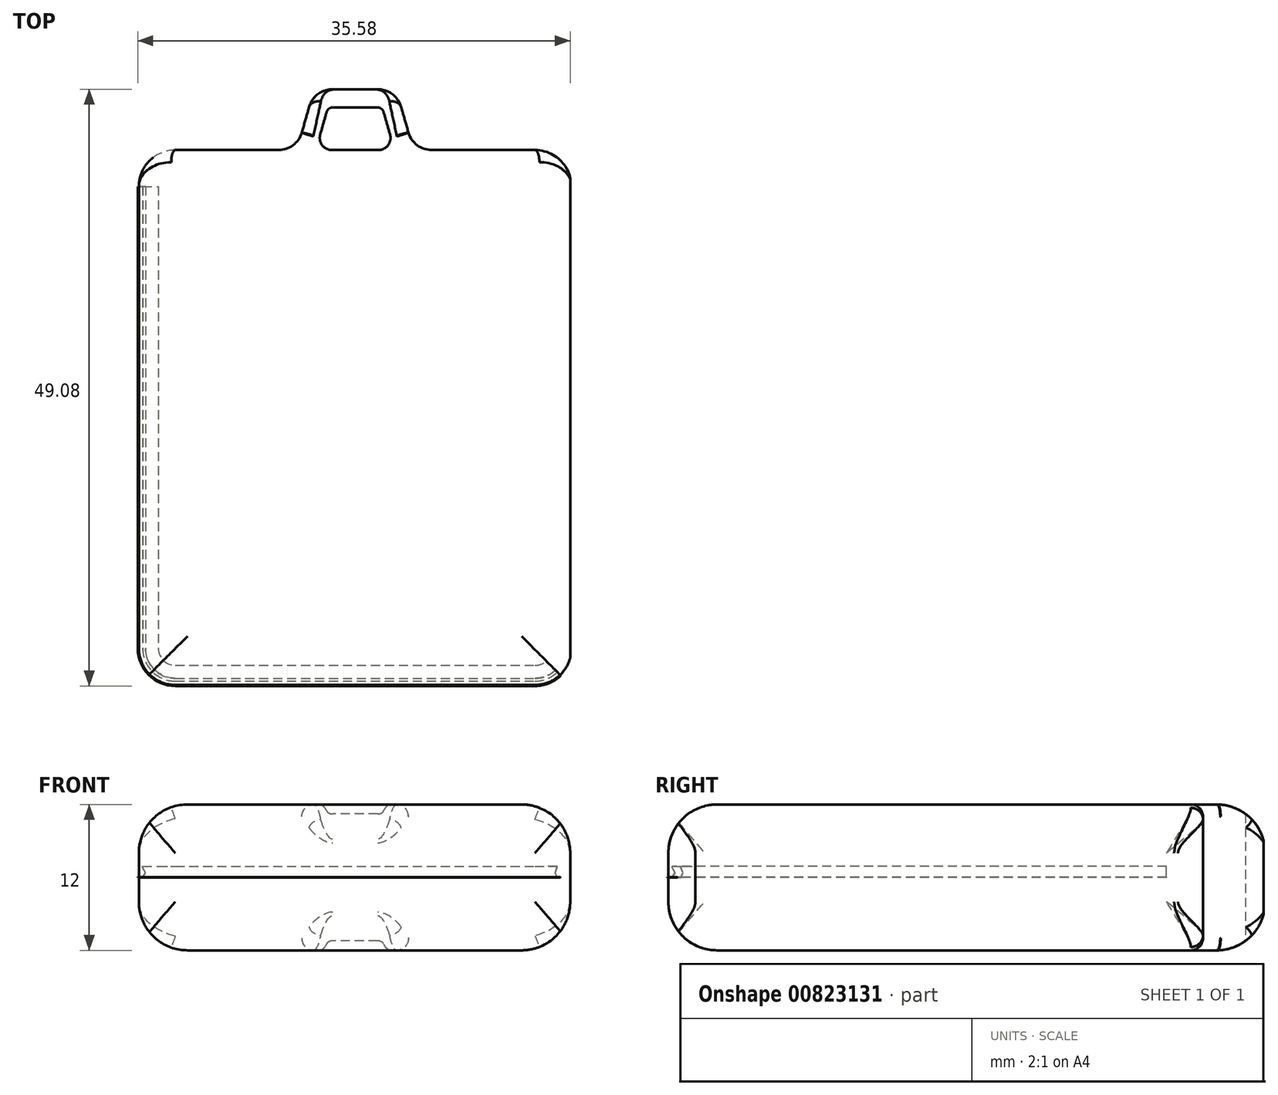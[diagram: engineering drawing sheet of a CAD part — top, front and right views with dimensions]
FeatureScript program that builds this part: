
annotation { "Feature Type Name" : "Feature", "Feature Type Description" : "" }
export const myFeature = defineFeature(function(context is Context, id is Id, definition is map)
    precondition{}
    {
        {
            var Q0;
            Q0=qCreatedBy(makeId("Top.planeOp"),FACE);
            var sketch = newSketch(context, id + "F0", { "sketchPlane" : qUnion([Q0])});
            skLineSegment(sketch, "E0.bottom", {"start": v(3, 0) * mm, "end": v(32.6, 0) * mm});
            skLineSegment(sketch, "E0.top", {"start": v(3, 44) * mm, "end": v(11.5, 44) * mm});
            skLineSegment(sketch, "E0.left", {"start": v(0, 3) * mm, "end": v(0, 41) * mm});
            skLineSegment(sketch, "E0.right", {"start": v(35.6, 3) * mm, "end": v(35.6, 41) * mm});
            skLineSegment(sketch, "E1", {"start": v(17.8, 62.18) * mm, "end": v(17.8, 0) * mm, "construction": true});
            skLineSegment(sketch, "E2", {"start": v(13.42, 45.45) * mm, "end": v(14.02, 47.55) * mm});
            skLineSegment(sketch, "E3", {"start": v(15.94, 49) * mm, "end": v(19.66, 49) * mm});
            skLineSegment(sketch, "E4", {"start": v(21.58, 47.55) * mm, "end": v(22.18, 45.45) * mm});
            skLineSegment(sketch, "E5.trimOffspring", {"start": v(24.1, 44) * mm, "end": v(32.6, 44) * mm});
            skPoint(sketch, "E6.visualSharp", {"position": v(13, 44) * mm});
            skArc(sketch, "E6.filletArc", {"start": v(11.5, 44) * mm, "mid": v(12.7, 44.4) * mm, "end": v(13.42, 45.45) * mm});
            skPoint(sketch, "E7.visualSharp", {"position": v(14.43, 49) * mm});
            skArc(sketch, "E7.filletArc", {"start": v(15.94, 49) * mm, "mid": v(14.74, 48.6) * mm, "end": v(14.02, 47.55) * mm});
            skPoint(sketch, "E8.visualSharp", {"position": v(21.17, 49) * mm});
            skArc(sketch, "E8.filletArc", {"start": v(21.58, 47.55) * mm, "mid": v(20.86, 48.6) * mm, "end": v(19.66, 49) * mm});
            skPoint(sketch, "E9.visualSharp", {"position": v(22.6, 44) * mm});
            skArc(sketch, "E9.filletArc", {"start": v(22.18, 45.45) * mm, "mid": v(22.9, 44.4) * mm, "end": v(24.1, 44) * mm});
            skLineSegment(sketch, "E10.0", {"start": v(15.94, 47.5) * mm, "end": v(19.66, 47.5) * mm});
            skLineSegment(sketch, "E11.0", {"start": v(14.93, 45.28) * mm, "end": v(15.46, 47.14) * mm});
            skLineSegment(sketch, "E12.0", {"start": v(20.14, 47.14) * mm, "end": v(20.67, 45.28) * mm});
            skLineSegment(sketch, "E13", {"start": v(15.89, 44) * mm, "end": v(19.71, 44) * mm});
            skPoint(sketch, "E14.visualSharp", {"position": v(15.56, 47.5) * mm});
            skArc(sketch, "E14.filletArc", {"start": v(15.94, 47.5) * mm, "mid": v(15.64, 47.4) * mm, "end": v(15.46, 47.14) * mm});
            skArc(sketch, "E15.filletArc", {"start": v(20.14, 47.14) * mm, "mid": v(19.96, 47.4) * mm, "end": v(19.66, 47.5) * mm});
            skPoint(sketch, "E16.visualSharp", {"position": v(21.04, 44) * mm});
            skArc(sketch, "E16.filletArc", {"start": v(19.71, 44) * mm, "mid": v(20.51, 44.4) * mm, "end": v(20.67, 45.28) * mm});
            skPoint(sketch, "E17.visualSharp", {"position": v(14.56, 44) * mm});
            skArc(sketch, "E17.filletArc", {"start": v(14.93, 45.28) * mm, "mid": v(15.09, 44.4) * mm, "end": v(15.89, 44) * mm});
            skPoint(sketch, "E18.visualSharp", {"position": v(0, 44) * mm});
            skArc(sketch, "E18.filletArc", {"start": v(3, 44) * mm, "mid": v(0.88, 43.12) * mm, "end": v(0, 41) * mm});
            skPoint(sketch, "E19.visualSharp", {"position": v(35.6, 44) * mm});
            skArc(sketch, "E19.filletArc", {"start": v(35.6, 41) * mm, "mid": v(34.72, 43.12) * mm, "end": v(32.6, 44) * mm});
            skPoint(sketch, "E20.visualSharp", {"position": v(35.6, 0) * mm});
            skArc(sketch, "E20.filletArc", {"start": v(32.6, 0) * mm, "mid": v(34.72, 0.88) * mm, "end": v(35.6, 3) * mm});
            skPoint(sketch, "E21.visualSharp", {"position": v(0, 0) * mm});
            skArc(sketch, "E21.filletArc", {"start": v(0, 3) * mm, "mid": v(0.88, 0.88) * mm, "end": v(3, 0) * mm});
            skSolve(sketch);
        }
        {
            var Q0;
            Q0 = qSketchRegion(id + "F0", true);
            extrude(context, id + "F1", {"entities" : qUnion([Q0]), "depth" : 12 * mm, "offsetDistance" : 25 * mm});
        }
        {
            var Q0;
            Q0=qCreatedBy(makeId("Front.planeOp"),FACE);
            var sketch = newSketch(context, id + "F2", { "sketchPlane" : qUnion([Q0])});
            skLineSegment(sketch, "E22.bottom", {"start": v(4, 0) * mm, "end": v(31.5, 0) * mm});
            skLineSegment(sketch, "E22.top", {"start": v(4, 12) * mm, "end": v(31.5, 12) * mm});
            skLineSegment(sketch, "E22.left", {"start": v(0, 4) * mm, "end": v(0, 8) * mm});
            skLineSegment(sketch, "E22.right", {"start": v(35.5, 4) * mm, "end": v(35.5, 8) * mm});
            skPoint(sketch, "E23.visualSharp", {"position": v(0, 12) * mm});
            skArc(sketch, "E23.filletArc", {"start": v(4, 12) * mm, "mid": v(1.17, 10.83) * mm, "end": v(0, 8) * mm});
            skPoint(sketch, "E24.visualSharp", {"position": v(0, 0) * mm});
            skArc(sketch, "E24.filletArc", {"start": v(0, 4) * mm, "mid": v(1.17, 1.17) * mm, "end": v(4, 0) * mm});
            skPoint(sketch, "E25.visualSharp", {"position": v(35.5, 0) * mm});
            skArc(sketch, "E25.filletArc", {"start": v(31.5, 0) * mm, "mid": v(34.33, 1.17) * mm, "end": v(35.5, 4) * mm});
            skPoint(sketch, "E26.visualSharp", {"position": v(35.5, 12) * mm});
            skArc(sketch, "E26.filletArc", {"start": v(35.5, 8) * mm, "mid": v(34.33, 10.83) * mm, "end": v(31.5, 12) * mm});
            skLineSegment(sketch, "E27.bottom", {"start": v(-3.14, 13.75) * mm, "end": v(38.49, 13.75) * mm});
            skLineSegment(sketch, "E27.top", {"start": v(-3.14, -2.53) * mm, "end": v(38.49, -2.53) * mm});
            skLineSegment(sketch, "E27.left", {"start": v(-3.14, 13.75) * mm, "end": v(-3.14, -2.53) * mm});
            skLineSegment(sketch, "E27.right", {"start": v(38.49, 13.75) * mm, "end": v(38.49, -2.53) * mm});
            skSolve(sketch);
        }
        {
            var Q0;
            Q0 = qSketchRegion(id + "F2", true);
            extrude(context, id + "F3", {"entities" : qUnion([Q0]), "operationType" : NewBodyOperationType.REMOVE, "endBound" : BoundingType.THROUGH_ALL, "oppositeDirection" : true, "depth" : 25 * mm, "offsetDistance" : 25 * mm});
        }
        {
            var Q0;
            Q0=qCreatedBy(makeId("Right.planeOp"),FACE);
            var sketch = newSketch(context, id + "F4", { "sketchPlane" : qUnion([Q0])});
            skLineSegment(sketch, "E28.bottom", {"start": v(4, 0) * mm, "end": v(45.12, 0) * mm});
            skLineSegment(sketch, "E28.top", {"start": v(4, 12) * mm, "end": v(45.12, 12) * mm});
            skLineSegment(sketch, "E28.left", {"start": v(0, 4) * mm, "end": v(0, 8) * mm});
            skLineSegment(sketch, "E28.right", {"start": v(49.12, 4) * mm, "end": v(49.12, 8) * mm});
            skPoint(sketch, "E29.visualSharp", {"position": v(49.12, 0) * mm});
            skArc(sketch, "E29.filletArc", {"start": v(45.12, 0) * mm, "mid": v(47.95, 1.17) * mm, "end": v(49.12, 4) * mm});
            skPoint(sketch, "E30.visualSharp", {"position": v(0, 0) * mm});
            skArc(sketch, "E30.filletArc", {"start": v(0, 4) * mm, "mid": v(1.17, 1.17) * mm, "end": v(4, 0) * mm});
            skPoint(sketch, "E31.visualSharp", {"position": v(0, 12) * mm});
            skArc(sketch, "E31.filletArc", {"start": v(4, 12) * mm, "mid": v(1.17, 10.83) * mm, "end": v(0, 8) * mm});
            skPoint(sketch, "E32.visualSharp", {"position": v(49.12, 12) * mm});
            skArc(sketch, "E32.filletArc", {"start": v(49.12, 8) * mm, "mid": v(47.95, 10.83) * mm, "end": v(45.12, 12) * mm});
            skLineSegment(sketch, "E33.bottom", {"start": v(51.83, -3.61) * mm, "end": v(-3.85, -3.61) * mm});
            skLineSegment(sketch, "E33.top", {"start": v(51.83, 17.86) * mm, "end": v(-3.85, 17.86) * mm});
            skLineSegment(sketch, "E33.left", {"start": v(51.83, -3.61) * mm, "end": v(51.83, 17.86) * mm});
            skLineSegment(sketch, "E33.right", {"start": v(-3.85, -3.61) * mm, "end": v(-3.85, 17.86) * mm});
            skSolve(sketch);
        }
        {
            var Q0;
            Q0 = qSketchRegion(id + "F4", true);
            extrude(context, id + "F5", {"entities" : qUnion([Q0]), "operationType" : NewBodyOperationType.REMOVE, "endBound" : BoundingType.THROUGH_ALL, "depth" : 25 * mm, "offsetDistance" : 25 * mm});
        }
        {
            var Q0;
            Q0=makeQuery(id+"F1.opExtrude","CAP_EDGE",EDGE,{"disambiguationData":[OSD([sQuery(id+"F0.wireOp",EDGE,"E0.top")])],"isStart":true});
            var Q1;
            Q1=makeQuery(id+"F1.opExtrude","CAP_EDGE",EDGE,{"disambiguationData":[OSD([sQuery(id+"F0.wireOp",EDGE,"E5.trimOffspring")])],"isStart":true});
            var Q2;
            Q2=makeQuery(id+"F1.opExtrude","CAP_EDGE",EDGE,{"disambiguationData":[OSD([sQuery(id+"F0.wireOp",EDGE,"E5.trimOffspring")])],"isStart":false});
            var Q3;
            Q3=makeQuery(id+"F1.opExtrude","CAP_EDGE",EDGE,{"disambiguationData":[OSD([sQuery(id+"F0.wireOp",EDGE,"E0.top")])],"isStart":false});
            fillet(context, id + "F6", {"entities" : qUnion([Q0, Q1, Q2, Q3]), "radius" : 1 * mm, "tangentPropagation" : true, "allowEdgeOverflow" : false});
        }
        {
            var Q0;
            Q0=qCreatedBy(makeId("Top.planeOp"),FACE);
            cPlane(context, id + "F7", {"entities" : qUnion([Q0]), "cplaneType" : CPlaneType.OFFSET, "offset" : 6 * mm, "width" : 150 * mm, "height" : 150 * mm});
        }
        {
            var Q0;
            Q0=qCreatedBy(makeId("Front.planeOp"),FACE);
            cPlane(context, id + "F8", {"entities" : qUnion([Q0]), "cplaneType" : CPlaneType.OFFSET, "offset" : 20 * mm, "oppositeDirection" : true, "width" : 150 * mm, "height" : 150 * mm});
        }
        {
            var Q0;
            Q0=qCreatedBy(id+"F8.planeOp",FACE);
            var sketch = newSketch(context, id + "F9", { "sketchPlane" : qUnion([Q0])});
            skLineSegment(sketch, "E34", {"start": v(0.31, 6) * mm, "end": v(0.54, 6.36) * mm});
            skLineSegment(sketch, "E35", {"start": v(0.54, 6.36) * mm, "end": v(0.31, 6.82) * mm});
            skLineSegment(sketch, "E36.0", {"start": v(0.32, 6) * mm, "end": v(0.55, 6.36) * mm});
            skLineSegment(sketch, "E37.0", {"start": v(0.55, 6.36) * mm, "end": v(0.32, 6.82) * mm});
            skLineSegment(sketch, "E38", {"start": v(0.32, 6.92) * mm, "end": v(1.6, 6.92) * mm});
            skLineSegment(sketch, "E39.0", {"start": v(0.32, 6.82) * mm, "end": v(0.32, 6.9) * mm});
            skLineSegment(sketch, "E40.0", {"start": v(0.32, 6.9) * mm, "end": v(1.6, 6.9) * mm});
            skLineSegment(sketch, "E41", {"start": v(0.31, 6.82) * mm, "end": v(0.31, 6.91) * mm});
            skLineSegment(sketch, "E42", {"start": v(0.31, 6) * mm, "end": v(-0.08, 6) * mm});
            skLineSegment(sketch, "E43", {"start": v(-0.08, 6) * mm, "end": v(-0.08, 6) * mm});
            skLineSegment(sketch, "E44", {"start": v(-0.08, 6) * mm, "end": v(0.32, 6) * mm});
            skPoint(sketch, "E45.visualSharp", {"position": v(0.32, 6.9) * mm});
            skArc(sketch, "E45.filletArc", {"start": v(0.32, 6.9) * mm, "mid": v(0.32, 6.9) * mm, "end": v(0.32, 6.9) * mm});
            skPoint(sketch, "E46.visualSharp", {"position": v(0.31, 6.92) * mm});
            skPoint(sketch, "E47.visualSharp", {"position": v(0.31, 6.82) * mm});
            skArc(sketch, "E47.filletArc", {"start": v(0.31, 6.82) * mm, "mid": v(0.31, 6.82) * mm, "end": v(0.31, 6.82) * mm});
            skPoint(sketch, "E48.visualSharp", {"position": v(0.32, 6.82) * mm});
            skArc(sketch, "E48.filletArc", {"start": v(0.32, 6.82) * mm, "mid": v(0.32, 6.82) * mm, "end": v(0.32, 6.82) * mm});
            skPoint(sketch, "E49.visualSharp", {"position": v(0.54, 6.36) * mm});
            skArc(sketch, "E49.filletArc", {"start": v(0.54, 6.36) * mm, "mid": v(0.54, 6.36) * mm, "end": v(0.54, 6.36) * mm});
            skPoint(sketch, "E50.visualSharp", {"position": v(0.55, 6.36) * mm});
            skArc(sketch, "E50.filletArc", {"start": v(0.55, 6.36) * mm, "mid": v(0.55, 6.36) * mm, "end": v(0.55, 6.36) * mm});
            skPoint(sketch, "E51.visualSharp", {"position": v(0.31, 6) * mm});
            skArc(sketch, "E51.filletArc", {"start": v(0.31, 6) * mm, "mid": v(0.31, 6) * mm, "end": v(0.31, 6) * mm});
            skPoint(sketch, "E52.visualSharp", {"position": v(0.32, 6) * mm});
            skArc(sketch, "E52.filletArc", {"start": v(0.32, 6) * mm, "mid": v(0.32, 6) * mm, "end": v(0.32, 6) * mm});
            skPoint(sketch, "E53.visualSharp", {"position": v(-0.08, 6) * mm});
            skArc(sketch, "E53.filletArc", {"start": v(-0.08, 6) * mm, "mid": v(-0.08, 6) * mm, "end": v(-0.08, 6) * mm});
            skPoint(sketch, "E54.visualSharp", {"position": v(1.6, 6.9) * mm});
            skArc(sketch, "E54.filletArc", {"start": v(1.6, 6.9) * mm, "mid": v(1.6, 6.9) * mm, "end": v(1.6, 6.9) * mm});
            skPoint(sketch, "E55.visualSharp", {"position": v(1.6, 6.92) * mm});
            skArc(sketch, "E55.filletArc", {"start": v(1.6, 6.92) * mm, "mid": v(1.6, 6.92) * mm, "end": v(1.6, 6.92) * mm});
            skLineSegment(sketch, "E56", {"start": v(1.6, 6.9) * mm, "end": v(1.6, 6.92) * mm});
            skArc(sketch, "E57.filletArc", {"start": v(0.32, 6.92) * mm, "mid": v(0.31, 6.92) * mm, "end": v(0.31, 6.91) * mm});
            skSolve(sketch);
        }
        {
            var Q0;
            Q0=qCreatedBy(id+"F7.planeOp",FACE);
            var sketch = newSketch(context, id + "F10", { "sketchPlane" : qUnion([Q0])});
            skLineSegment(sketch, "E58.0", {"start": v(0, 41) * mm, "end": v(0, 3) * mm});
            skArc(sketch, "E59.0", {"start": v(3, 0) * mm, "mid": v(0.88, 0.88) * mm, "end": v(0, 3) * mm});
            skLineSegment(sketch, "E60.0", {"start": v(32.6, 0) * mm, "end": v(3, 0) * mm});
            skArc(sketch, "E61.0", {"start": v(34.63, 0.8) * mm, "mid": v(33.69, 0.21) * mm, "end": v(32.6, 0) * mm});
            skSolve(sketch);
        }
        {
            var Q0;
            Q0 = qSketchRegion(id + "F9", true);
            var Q1;
            Q1 = qConstructionFilter(qBodyType(qCreatedBy(id + "F10" ,EDGE), BodyType.WIRE), ConstructionObject.NO);
            sweep(context, id + "F11", {"profiles" : qUnion([Q0]), "path" : qUnion([Q1])});
        }
    });
